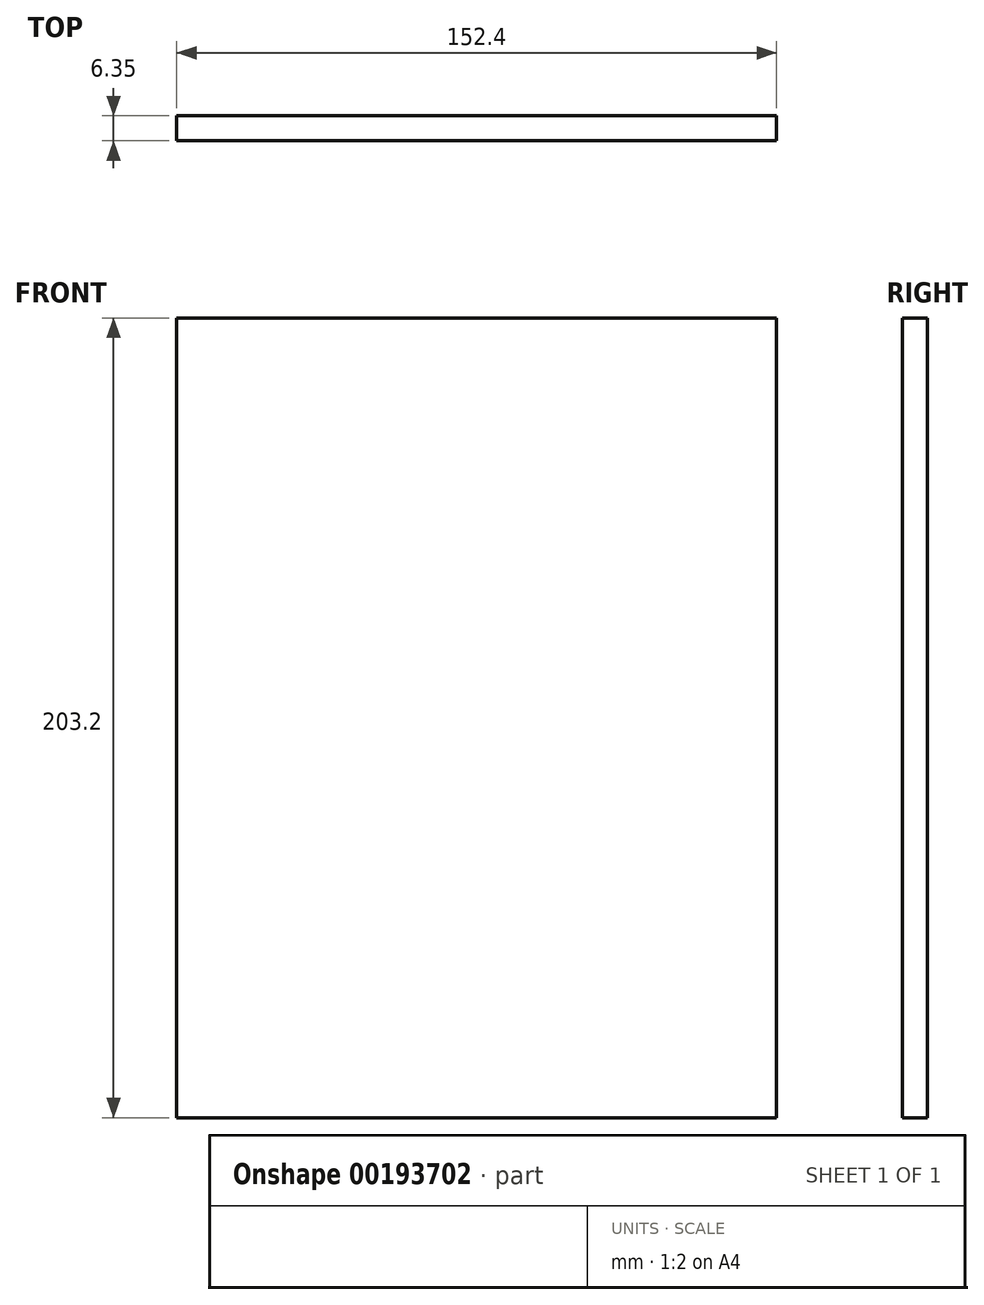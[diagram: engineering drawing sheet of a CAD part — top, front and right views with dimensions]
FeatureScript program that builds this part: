
annotation { "Feature Type Name" : "Feature", "Feature Type Description" : "" }
export const myFeature = defineFeature(function(context is Context, id is Id, definition is map)
    precondition{}
    {
        {
            var Q0;
            Q0=qCreatedBy(makeId("Front.planeOp"),FACE);
            var sketch = newSketch(context, id + "F0", { "sketchPlane" : qUnion([Q0])});
            skLineSegment(sketch, "E0.bottom", {"start": v(4001.77, -1606.25) * mm, "end": v(4270.25, -1606.25) * mm});
            skLineSegment(sketch, "E0.top", {"start": v(4001.77, -1820.74) * mm, "end": v(4270.25, -1820.74) * mm});
            skLineSegment(sketch, "E0.left", {"start": v(4001.77, -1606.25) * mm, "end": v(4001.77, -1820.74) * mm});
            skLineSegment(sketch, "E0.right", {"start": v(4270.25, -1606.25) * mm, "end": v(4270.25, -1820.74) * mm});
            skLineSegment(sketch, "E1.bottom", {"start": v(76.2, -101.6) * mm, "end": v(-76.2, -101.6) * mm});
            skLineSegment(sketch, "E1.top", {"start": v(76.2, 101.6) * mm, "end": v(-76.2, 101.6) * mm});
            skLineSegment(sketch, "E1.left", {"start": v(76.2, -101.6) * mm, "end": v(76.2, 101.6) * mm});
            skLineSegment(sketch, "E1.right", {"start": v(-76.2, -101.6) * mm, "end": v(-76.2, 101.6) * mm});
            skPoint(sketch, "E1.middle", {"position": v(0, 0) * mm});
            skSolve(sketch);
        }
        {
            var Q0;
            Q0=makeQuery(id+"F0.imprint","IMPRINT",FACE,{"disambiguationData":[TD([[makeQuery(id+"F0.imprint","IMPRINT",EDGE,{"derivedFrom":sQuery(id+"F0.wireOp",EDGE,"E1.bottom")}),-1.0]])]});
            extrude(context, id + "F1", {"entities" : qUnion([Q0]), "depth" : 6.35 * mm});
        }
    });
